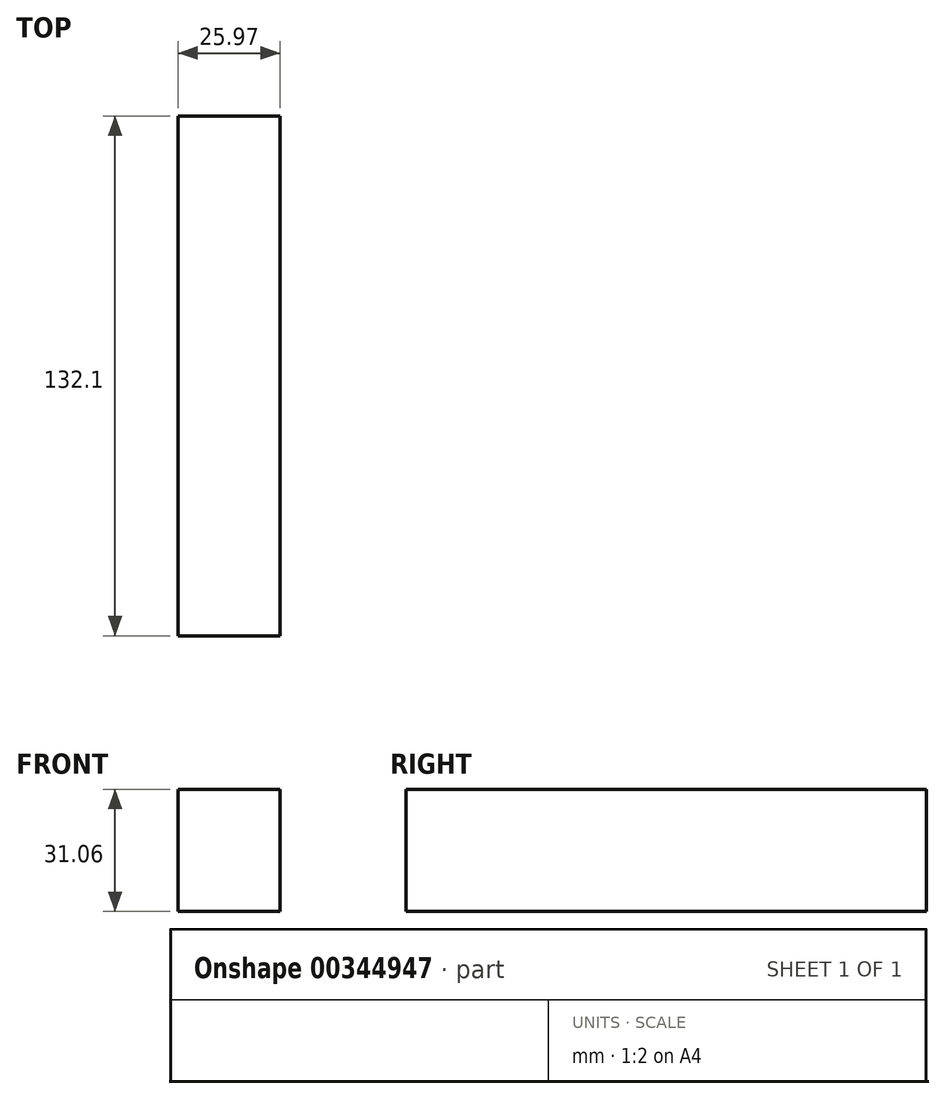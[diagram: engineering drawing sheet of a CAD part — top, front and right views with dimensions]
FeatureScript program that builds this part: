
annotation { "Feature Type Name" : "Feature", "Feature Type Description" : "" }
export const myFeature = defineFeature(function(context is Context, id is Id, definition is map)
    precondition{}
    {
        {
            var Q0;
            Q0=qCreatedBy(makeId("Front.planeOp"),FACE);
            var sketch = newSketch(context, id + "F0", { "sketchPlane" : qUnion([Q0])});
            skLineSegment(sketch, "E0.bottom", {"start": v(0, 0) * mm, "end": v(-25.97, 0) * mm});
            skLineSegment(sketch, "E0.top", {"start": v(0, -31.06) * mm, "end": v(-25.97, -31.06) * mm});
            skLineSegment(sketch, "E0.left", {"start": v(0, 0) * mm, "end": v(0, -31.06) * mm});
            skLineSegment(sketch, "E0.right", {"start": v(-25.97, 0) * mm, "end": v(-25.97, -31.06) * mm});
            skSolve(sketch);
        }
        {
            var Q0;
            Q0=makeQuery(id+"F0.imprint","IMPRINT",FACE,{"disambiguationData":[TD([[makeQuery(id+"F0.imprint","IMPRINT",EDGE,{"derivedFrom":sQuery(id+"F0.wireOp",EDGE,"E0.bottom")}),1.0]])]});
            extrude(context, id + "F1", {"entities" : qUnion([Q0]), "depth" : 132.1 * mm});
        }
        {
            var Q0;
            Q0=makeQuery(id+"F1.opExtrude","SWEPT_BODY",BODY,{"disambiguationData":[OSD([sQuery(id+"F0.wireOp",EDGE,"E0.bottom"),sQuery(id+"F0.wireOp",EDGE,"E0.top"),sQuery(id+"F0.wireOp",EDGE,"E0.left"),sQuery(id+"F0.wireOp",EDGE,"E0.right")])]});
            var Q1;
            Q1=makeQuery(id+"F1.opExtrude","SWEPT_EDGE",EDGE,{"disambiguationData":[OSD([sQuery(id+"F0.wireOp",EDGE,"E0.bottom"),sQuery(id+"F0.wireOp",EDGE,"E0.left")])]});
            transform(context, id + "F2", {"entities" : qUnion([Q0]), "transformType" : TransformType.ROTATION, "transformAxis" : qUnion([Q1]), "angle" : 180 * degree, "oppositeDirection" : true, "makeCopy" : false});
        }
    });
